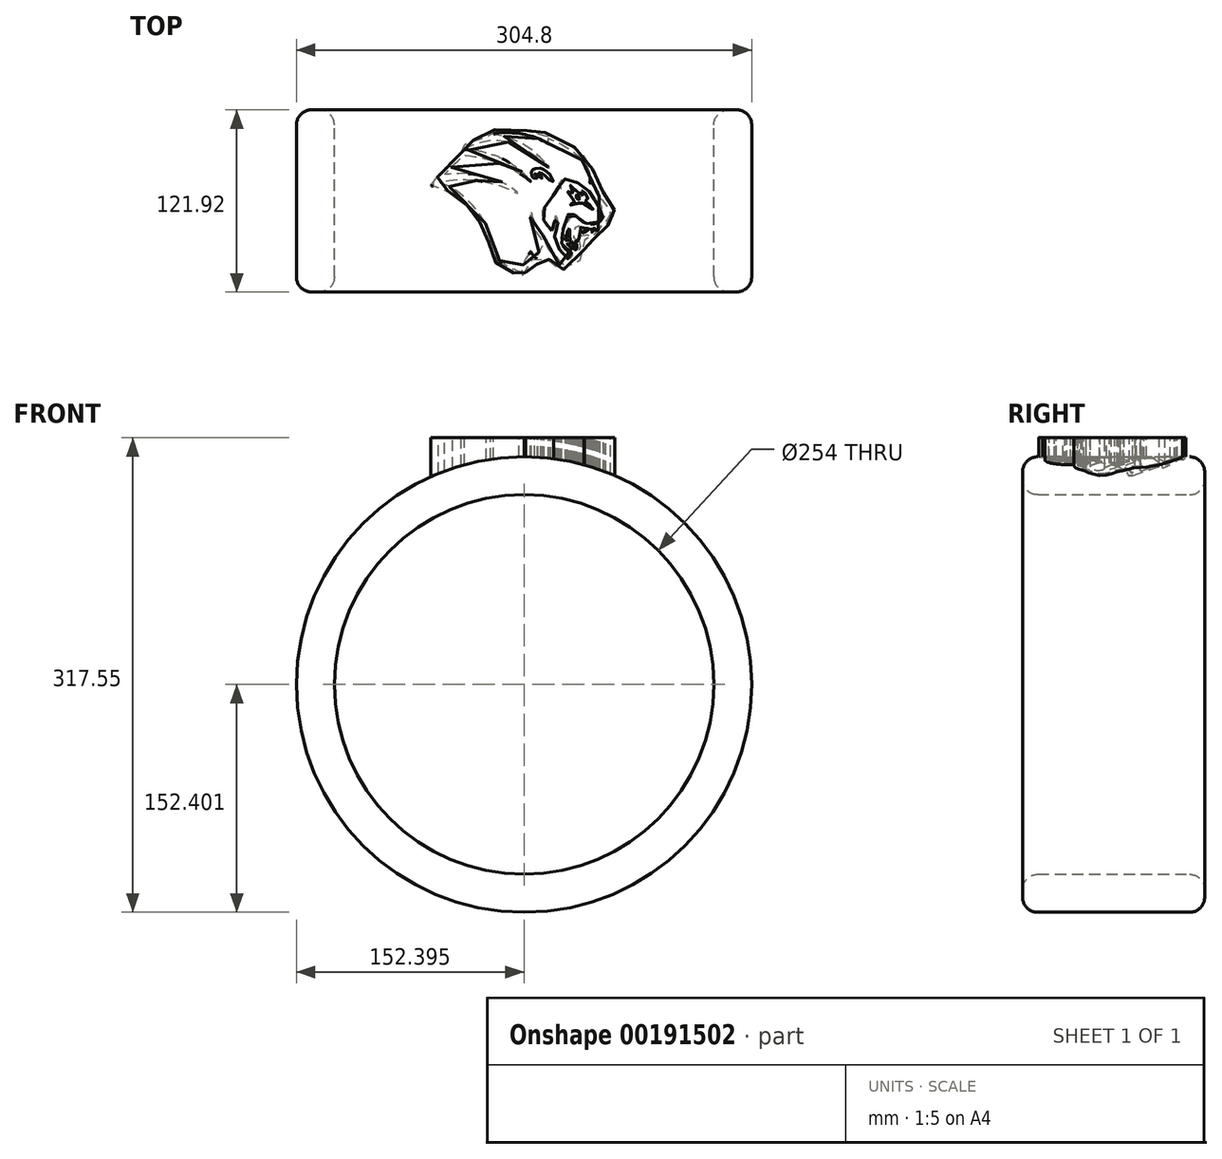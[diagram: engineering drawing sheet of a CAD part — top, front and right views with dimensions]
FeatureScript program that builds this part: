
annotation { "Feature Type Name" : "Feature", "Feature Type Description" : "" }
export const myFeature = defineFeature(function(context is Context, id is Id, definition is map)
    precondition{}
    {
        {
            var Q0;
            Q0=qCreatedBy(makeId("Top.planeOp"),FACE);
            var sketch = newSketch(context, id + "F0", { "sketchPlane" : qUnion([Q0])});
            skFitSpline(sketch, "E0", {"points": [v(-31.09, 27.1) * mm, v(-31.11, 27.15) * mm, v(-36.69, 27.23) * mm, v(-36.69, 27.24) * mm, v(-35.85, 28.2) * mm, v(-34.33, 29.39) * mm, v(-29.23, 32.47) * mm, v(-22.89, 35.49) * mm, v(-13.94, 37.95) * mm, v(-11.34, 38.16) * mm, v(-11.31, 38.2) * mm, v(-14.28, 41.78) * mm, v(-14.26, 41.81) * mm, v(-10.6, 42.33) * mm, v(-7.43, 42.66) * mm, v(-3.17, 42.95) * mm, v(2.4, 43.06) * mm, v(7.16, 42.72) * mm, v(11.67, 42.16) * mm, v(14.33, 41.53) * mm, v(16.85, 40.84) * mm, v(19.9, 39.76) * mm, v(22.88, 38.53) * mm, v(24.4, 37.68) * mm, v(24.45, 37.7) * mm, v(24.02, 40.9) * mm, v(24.02, 40.93) * mm, v(28.38, 39.57) * mm, v(33.53, 37.41) * mm, v(37.52, 35.36) * mm, v(40.75, 33.62) * mm, v(43.89, 31.64) * mm, v(46.7, 29.43) * mm, v(50, 26.6) * mm, v(52.22, 23.95) * mm, v(54.14, 21.65) * mm, v(55.69, 18.98) * mm, v(56.9, 15.92) * mm, v(57.83, 12.7) * mm, v(57.85, 9) * mm, v(57.85, 8.32) * mm, v(57.86, 8.31) * mm, v(60.1, 6.1) * mm, v(61.52, 4.24) * mm, v(63.62, 1.45) * mm, v(65.26, -1.13) * mm, v(65.81, -2.07) * mm, v(65.78, -2.08) * mm, v(65.15, -2.57) * mm, v(65.18, -2.6) * mm, v(66.55, -4.08) * mm, v(68.27, -6.1) * mm, v(69.9, -8.32) * mm, v(71.5, -11.06) * mm, v(71.82, -11.68) * mm, v(71.88, -12.08) * mm, v(71.86, -12.64) * mm, v(71.76, -12.84) * mm, v(71.5, -14.05) * mm, v(71.24, -15.23) * mm, v(70.58, -16.82) * mm, v(69.65, -18.77) * mm, v(68.57, -20.04) * mm, v(67.66, -21.18) * mm, v(66.43, -22.39) * mm, v(65.23, -23.47) * mm, v(63.89, -24.57) * mm, v(63.22, -25.56) * mm, v(62.06, -27.1) * mm, v(60.99, -28.53) * mm, v(59.27, -29.8) * mm, v(57.18, -30.9) * mm, v(54.73, -31.73) * mm, v(52.52, -31.6) * mm, v(50.9, -30.96) * mm, v(50.9, -30.97) * mm, v(50.87, -31.5) * mm, v(51.34, -33.26) * mm, v(51.34, -35.4) * mm, v(51.33, -36.8) * mm, v(50.75, -38.7) * mm, v(49.66, -41.82) * mm, v(48.02, -45.67) * mm, v(44.56, -48.82) * mm, v(40.43, -50.61) * mm, v(37.24, -51.04) * mm, v(34.13, -50.7) * mm, v(30.98, -49.95) * mm, v(30.9, -49.89) * mm, v(32.88, -46.3) * mm, v(32.88, -46.25) * mm, v(28.95, -43.3) * mm, v(28.87, -43.33) * mm, v(28.38, -43.84) * mm, v(27.6, -44.27) * mm, v(26.31, -44.55) * mm, v(24.7, -44.6) * mm, v(22.84, -44.07) * mm, v(21.99, -43.54) * mm, v(21.96, -43.54) * mm, v(21.44, -44.81) * mm, v(20.64, -46.8) * mm, v(20.12, -48.33) * mm, v(20.04, -48.36) * mm, v(18.66, -46.98) * mm, v(17.36, -45.7) * mm, v(16.25, -44.55) * mm, v(15.52, -43.7) * mm, v(15.46, -43.72) * mm, v(14.85, -45.07) * mm, v(13.48, -47.58) * mm, v(12.46, -51.1) * mm, v(12.05, -54.2) * mm, v(12.03, -54.4) * mm, v(11.18, -54.5) * mm, v(11.18, -54.55) * mm, v(11.2, -55.19) * mm, v(11.1, -55.14) * mm, v(10.87, -55.15) * mm, v(8.8, -54.63) * mm, v(7.63, -54.5) * mm, v(6.57, -54.15) * mm, v(5.53, -53.84) * mm, v(4.92, -53.54) * mm, v(3.78, -53.1) * mm, v(2.58, -52.38) * mm, v(2.44, -52.14) * mm, v(0.55, -52.17) * mm, v(-0.92, -51.3) * mm, v(-2.65, -50.3) * mm, v(-4.37, -49.16) * mm, v(-6.14, -47.9) * mm, v(-8.37, -45.72) * mm, v(-8.8, -45.36) * mm, v(-9.07, -44.63) * mm, v(-9.78, -41.7) * mm, v(-10.31, -39.55) * mm, v(-10.83, -37.7) * mm, v(-11.39, -35.7) * mm, v(-12.15, -33.5) * mm, v(-13.05, -31.4) * mm, v(-13.76, -29.67) * mm, v(-14.56, -27.42) * mm, v(-15.32, -25.69) * mm, v(-16.12, -23.85) * mm, v(-16.99, -22.43) * mm, v(-17.61, -20.96) * mm, v(-19.36, -18.15) * mm, v(-20.1, -17.04) * mm, v(-21.13, -15.53) * mm, v(-21.6, -14.82) * mm, v(-23.16, -12.67) * mm, v(-24.28, -11.21) * mm, v(-25.5, -9.91) * mm, v(-26.57, -8.6) * mm, v(-28.06, -7.07) * mm, v(-29.57, -5.48) * mm, v(-31.18, -4.23) * mm, v(-32.48, -3.02) * mm, v(-35.01, -1) * mm, v(-37.93, 0.76) * mm, v(-39.68, 1.63) * mm, v(-43.52, 3.41) * mm, v(-47.16, 4.49) * mm, v(-51.45, 5.15) * mm, v(-51.45, 5.22) * mm, v(-50, 7.18) * mm, v(-47.7, 9.98) * mm, v(-45.1, 13.07) * mm, v(-41.63, 16.66) * mm, v(-37.44, 21.13) * mm, v(-34.27, 24.1) * mm, v(-31.09, 27.1) * mm]});
            skFitSpline(sketch, "E1", {"points": [v(-14.87, -19.96) * mm, v(-16.53, -17.13) * mm, v(-18.86, -13.58) * mm, v(-21.78, -9.61) * mm, v(-24.55, -6.73) * mm, v(-29.24, -2.2) * mm, v(-33.32, 1.06) * mm, v(-37.46, 3.8) * mm, v(-40.9, 5.46) * mm, v(-43.35, 6.3) * mm, v(-45.8, 6.8) * mm, v(-46.1, 7) * mm, v(-45.1, 7.59) * mm, v(-39.68, 8.6) * mm, v(-34.05, 9.1) * mm, v(-26.3, 9.07) * mm, v(-20, 8.52) * mm, v(-11.98, 6.95) * mm, v(-2.95, 4.5) * mm, v(7.46, -0.37) * mm, v(7.58, -0.43) * mm, v(5.39, 1.58) * mm, v(1.22, 4.64) * mm, v(-6.3, 8.72) * mm, v(-13.47, 10.97) * mm, v(-20.35, 12.54) * mm, v(-32.07, 13.18) * mm, v(-42.1, 12.72) * mm, v(-42, 12.83) * mm, v(-37.72, 17.5) * mm, v(-31.7, 23.1) * mm, v(-29.15, 25.2) * mm, v(-24.9, 25.08) * mm, v(-20.47, 24.47) * mm, v(-15.32, 23.36) * mm, v(-11.1, 22.1) * mm, v(-6, 20.24) * mm, v(-1.72, 18.52) * mm, v(2.27, 16.6) * mm, v(8.16, 13.3) * mm, v(13.4, 9.63) * mm, v(15.68, 7.8) * mm, v(15.68, 7.82) * mm, v(14.13, 9.77) * mm, v(12.1, 12.08) * mm, v(8.3, 15.63) * mm, v(5.1, 18.14) * mm, v(0.78, 20.85) * mm, v(-6.8, 24.67) * mm, v(-16.6, 27.67) * mm, v(-19.8, 28.49) * mm, v(-23.88, 28.93) * mm, v(-27.84, 29.13) * mm, v(-28.83, 29.25) * mm, v(-28.25, 30.03) * mm, v(-24.92, 31.85) * mm, v(-18.83, 34.06) * mm, v(-13.56, 35.28) * mm, v(-9.07, 35.69) * mm, v(-3.03, 35.3) * mm, v(3.32, 33.44) * mm, v(8.22, 31.43) * mm, v(14.57, 27.73) * mm, v(19.8, 23.97) * mm, v(25.5, 18.58) * mm, v(29.06, 15.28) * mm, v(29.06, 15.31) * mm, v(27.98, 16.94) * mm, v(25.97, 19.45) * mm, v(22.94, 23.1) * mm, v(19.59, 26.07) * mm, v(16.79, 28.66) * mm, v(12.12, 32.04) * mm, v(7.7, 34.26) * mm, v(0, 37.44) * mm, v(-4.46, 38.57) * mm, v(-9.33, 39.6) * mm, v(-9.3, 39.74) * mm, v(-7.35, 40.32) * mm, v(1.8, 40.56) * mm, v(8.65, 39.94) * mm, v(15.65, 38.31) * mm, v(20.75, 36.65) * mm, v(27.72, 32.86) * mm, v(27.72, 32.89) * mm, v(27.46, 36.7) * mm, v(27.52, 36.77) * mm, v(31.83, 34.93) * mm, v(36.67, 32.57) * mm, v(42.64, 28.75) * mm, v(48.47, 24.06) * mm, v(52.7, 18.98) * mm, v(54.89, 13.8) * mm, v(55.33, 9.69) * mm, v(55.18, 7.18) * mm, v(55.27, 7.1) * mm, v(57.42, 4.85) * mm, v(60.51, 1.35) * mm, v(61.91, -0.72) * mm, v(61.88, -0.8) * mm, v(60.78, -1.71) * mm, v(60.9, -1.8) * mm, v(63.2, -4.3) * mm, v(66.14, -7.78) * mm, v(68.88, -11.92) * mm, v(68.9, -13.05) * mm, v(68.27, -15.24) * mm, v(66.37, -18.42) * mm, v(63.66, -21.24) * mm, v(62.06, -22.18) * mm, v(62.03, -22.43) * mm, v(60.9, -24.65) * mm, v(58.62, -26.9) * mm, v(55.24, -28.88) * mm, v(52.93, -29.11) * mm, v(52.9, -28.97) * mm, v(54.07, -26.96) * mm, v(53.95, -27.07) * mm, v(52.2, -28.1) * mm, v(50.31, -28.74) * mm, v(46.46, -28.82) * mm, v(46.5, -28.65) * mm, v(49.67, -22.96) * mm, v(49.32, -22.67) * mm, v(48.18, -21.97) * mm, v(47.13, -20.96) * mm, v(47.05, -20.96) * mm, v(46.7, -21.42) * mm, v(45.15, -23.14) * mm, v(44.22, -23.85) * mm, v(44.1, -24.19) * mm, v(44.19, -29.7) * mm, v(44.22, -29.7) * mm, v(44.92, -28.76) * mm, v(44.95, -28.8) * mm, v(45.44, -29.35) * mm, v(45.8, -30.37) * mm, v(45.9, -32.23) * mm, v(46, -32.23) * mm, v(47.48, -30.69) * mm, v(47.54, -30.69) * mm, v(47.98, -31.21) * mm, v(48.42, -32.87) * mm, v(48.68, -36.43) * mm, v(47.54, -38.62) * mm, v(47.37, -39.43) * mm, v(46.46, -42.26) * mm, v(44.66, -45.2) * mm, v(41.97, -47.1) * mm, v(38.65, -48.03) * mm, v(34.77, -47.92) * mm, v(34.74, -47.86) * mm, v(36.17, -45.32) * mm, v(36.17, -45.26) * mm, v(34.07, -43.66) * mm, v(30.98, -41.07) * mm, v(29.12, -39.32) * mm, v(27.14, -36.66) * mm, v(26.2, -34.83) * mm, v(25.45, -32.87) * mm, v(24.9, -30.05) * mm, v(24.75, -28.85) * mm, v(24.66, -28.8) * mm, v(23.29, -27.54) * mm, v(21.74, -25.69) * mm, v(20.52, -23.85) * mm, v(18.68, -20.22) * mm, v(17.37, -17.45) * mm, v(16.55, -14.63) * mm, v(15.91, -12.2) * mm, v(15.77, -9.76) * mm, v(15.68, -9.76) * mm, v(15.36, -12.64) * mm, v(15.27, -16.23) * mm, v(16.12, -20.1) * mm, v(17.46, -23.43) * mm, v(19.24, -26.14) * mm, v(22.06, -29.32) * mm, v(22.27, -29.52) * mm, v(22.3, -30.95) * mm, v(22.73, -33.22) * mm, v(23.96, -35.85) * mm, v(23.93, -36) * mm, v(22.82, -36.98) * mm, v(20.93, -39.55) * mm, v(19.88, -41.24) * mm, v(19.24, -43.28) * mm, v(19.1, -43.4) * mm, v(18.57, -43.08) * mm, v(17.87, -42.17) * mm, v(17.08, -41.15) * mm, v(16.06, -39.6) * mm, v(15.65, -38.9) * mm, v(15.62, -38.94) * mm, v(14.51, -40.3) * mm, v(13.32, -42.03) * mm, v(11.95, -44.27) * mm, v(11.07, -46.34) * mm, v(10.35, -48.41) * mm, v(9.62, -50.86) * mm, v(9.35, -52.58) * mm, v(9.3, -52.58) * mm, v(7.52, -52.23) * mm, v(6.06, -51.74) * mm, v(4.14, -50.95) * mm, v(2.62, -50.28) * mm, v(0.46, -49.2) * mm, v(-0.88, -48.32) * mm, v(-2.69, -47.13) * mm, v(-4.06, -46.14) * mm, v(-5.37, -45) * mm, v(-6.5, -43.86) * mm, v(-7.09, -43.08) * mm, v(-7.35, -41.82) * mm, v(-7.58, -39.96) * mm, v(-8.43, -37.07) * mm, v(-9.27, -34.13) * mm, v(-10.79, -29.55) * mm, v(-12.22, -25.9) * mm, v(-14.26, -21.53) * mm, v(-14.87, -19.96) * mm]});
            skFitSpline(sketch, "E2", {"points": [v(20.64, 14.12) * mm, v(21.76, 13.88) * mm, v(23.17, 13.2) * mm, v(24.26, 12.5) * mm, v(25.27, 11.74) * mm, v(26.44, 10.52) * mm, v(27.07, 9.84) * mm, v(27.64, 9.1) * mm, v(27.7, 9.06) * mm, v(30.4, 7.75) * mm, v(30.5, 7.73) * mm, v(30.46, 7.97) * mm, v(30.13, 9) * mm, v(29.51, 10.69) * mm, v(28.86, 12.03) * mm, v(27.76, 13.35) * mm, v(26.8, 14.2) * mm, v(25.54, 15.12) * mm, v(24.24, 15.9) * mm, v(23, 16.5) * mm, v(21.47, 16.84) * mm, v(19.08, 16.75) * mm, v(17.8, 16.44) * mm, v(16.92, 15.9) * mm, v(16.42, 15.22) * mm, v(16.11, 14.43) * mm, v(15.98, 12.98) * mm, v(16.3, 11.89) * mm, v(16.76, 11.13) * mm, v(17.4, 10.34) * mm, v(17.5, 10.21) * mm, v(20.2, 10.12) * mm, v(20.2, 10.16) * mm, v(20, 10.47) * mm, v(19.46, 11.3) * mm, v(18.95, 11.9) * mm, v(18.42, 12.67) * mm, v(18.18, 13.08) * mm, v(18.18, 13.1) * mm, v(18.77, 12.97) * mm, v(20.42, 12.07) * mm, v(21.6, 11.22) * mm, v(23.34, 10) * mm, v(23.4, 10.01) * mm, v(23.45, 10.34) * mm, v(22.77, 11.31) * mm, v(21.82, 12.43) * mm, v(21.06, 13.19) * mm, v(20.47, 13.8) * mm, v(20.36, 14.07) * mm, v(20.64, 14.12) * mm]});
            skFitSpline(sketch, "E3", {"points": [v(29.5, -24.96) * mm, v(28.58, -24.35) * mm, v(27.6, -23.28) * mm, v(26.55, -21.99) * mm, v(25.54, -20.52) * mm, v(24.7, -18.86) * mm, v(23.88, -16.81) * mm, v(23.47, -15.09) * mm, v(22.99, -12.75) * mm, v(23.1, -12.53) * mm, v(23.95, -10.91) * mm, v(24.86, -9.04) * mm, v(25.75, -7.35) * mm, v(26.7, -5.8) * mm, v(27.88, -4.41) * mm, v(29.43, -2.66) * mm, v(31.27, -0.9) * mm, v(33.27, 0.81) * mm, v(35.98, 3.21) * mm, v(35.98, 3.28) * mm, v(35.63, 3.76) * mm, v(35.07, 4.35) * mm, v(34.8, 4.96) * mm, v(34.63, 5.81) * mm, v(34.7, 7.06) * mm, v(34.93, 7.73) * mm, v(35.94, 8.78) * mm, v(36.81, 9.33) * mm, v(38.01, 9.61) * mm, v(39.35, 9.66) * mm, v(40.85, 9.42) * mm, v(42.3, 9.1) * mm, v(43.98, 8.55) * mm, v(45.84, 7.68) * mm, v(47.83, 6.54) * mm, v(49.9, 5.2) * mm, v(51.6, 3.98) * mm, v(52.98, 2.8) * mm, v(53.93, 1.93) * mm, v(55, 0.77) * mm, v(56.05, -0.54) * mm, v(56.03, -0.56) * mm, v(54.65, -1.24) * mm, v(54.76, -1.3) * mm, v(56.03, -2.2) * mm, v(57.65, -3.42) * mm, v(59.34, -4.88) * mm, v(61.47, -7.1) * mm, v(63.04, -8.9) * mm, v(64.22, -10.48) * mm, v(64.2, -10.5) * mm, v(59.74, -11.02) * mm, v(59.72, -11.02) * mm, v(59.74, -11.42) * mm, v(59.9, -11.48) * mm, v(60.57, -11.75) * mm, v(62.04, -12.36) * mm, v(62.65, -12.6) * mm, v(62.67, -12.62) * mm, v(62.71, -13.34) * mm, v(62.89, -13.71) * mm, v(63.48, -14.6) * mm, v(64.22, -15.52) * mm, v(64.24, -15.74) * mm, v(63.94, -16.3) * mm, v(63.43, -17) * mm, v(62.73, -17.9) * mm, v(61.93, -18.67) * mm, v(60.8, -19.43) * mm, v(59.6, -19.98) * mm, v(58.43, -20.37) * mm, v(57.17, -20.61) * mm, v(54.26, -20.46) * mm, v(52.54, -20.04) * mm, v(51.49, -19.56) * mm, v(49.87, -18.62) * mm, v(48.5, -17.51) * mm, v(47.3, -16.44) * mm, v(45.88, -15.17) * mm, v(44.76, -14.52) * mm, v(44.04, -14.3) * mm, v(41.64, -14.17) * mm, v(40.04, -14.54) * mm, v(39.04, -15.41) * mm, v(39.08, -15.44) * mm, v(41.8, -16.57) * mm, v(41.82, -16.65) * mm, v(40.93, -18) * mm, v(39.82, -19.8) * mm, v(38.1, -22.76) * mm, v(36.88, -24.94) * mm, v(36.12, -27.16) * mm, v(35.87, -29.14) * mm, v(35.87, -32.06) * mm, v(36.24, -33.32) * mm, v(37, -35.08) * mm, v(38.26, -36.67) * mm, v(39.49, -37.84) * mm, v(41.2, -39.1) * mm, v(42.76, -39.92) * mm, v(43.55, -40.27) * mm, v(43.61, -40.33) * mm, v(43.34, -41.19) * mm, v(42.78, -42.37) * mm, v(41.7, -43.5) * mm, v(39.96, -44.59) * mm, v(39.96, -44.57) * mm, v(40.25, -43.87) * mm, v(40.3, -43.77) * mm, v(39.86, -43.27) * mm, v(38.83, -42.37) * mm, v(37.58, -41.13) * mm, v(36.04, -39.4) * mm, v(34.86, -37.76) * mm, v(33.78, -36.12) * mm, v(32.58, -33.71) * mm, v(31.7, -31.43) * mm, v(31.06, -29.18) * mm, v(31.06, -29.1) * mm, v(31.73, -28.48) * mm, v(32.62, -26.8) * mm, v(33.3, -25.15) * mm, v(33.67, -23.64) * mm, v(33.9, -21.67) * mm, v(33.87, -19.43) * mm, v(33.67, -17.84) * mm, v(33.1, -16.36) * mm, v(31.92, -14.6) * mm, v(31.92, -14.67) * mm, v(31.88, -16.13) * mm, v(31.92, -18.77) * mm, v(31.78, -19.78) * mm, v(31.5, -21.26) * mm, v(31.1, -22.48) * mm, v(30.62, -23.69) * mm, v(29.88, -24.82) * mm, v(29.5, -24.96) * mm]});
            skFitSpline(sketch, "E4", {"points": [v(40.24, 1.17) * mm, v(41.09, 1.11) * mm, v(42.05, 0.77) * mm, v(43.01, 0.27) * mm, v(43.68, -0.31) * mm, v(43.77, -0.37) * mm, v(43.8, 1) * mm, v(43.65, 1.35) * mm, v(43.27, 2.1) * mm, v(42.6, 3.4) * mm, v(41.96, 5.37) * mm, v(42.05, 5.43) * mm, v(42.72, 4.67) * mm, v(43.89, 3.5) * mm, v(45.58, 2.16) * mm, v(47.44, 0.68) * mm, v(50.56, -1.77) * mm, v(50.56, -1.74) * mm, v(50.45, -0.63) * mm, v(50.15, 0.77) * mm, v(49.98, 1.84) * mm, v(50.04, 1.9) * mm, v(50.82, 1.2) * mm, v(51.79, 0.27) * mm, v(52.9, -1.04) * mm, v(54.06, -3.64) * mm, v(54.03, -3.78) * mm, v(52.34, -5.3) * mm, v(52.34, -5.56) * mm, v(53.83, -6.4) * mm, v(55.81, -8.48) * mm, v(57.2, -10.46) * mm, v(57.3, -10.9) * mm, v(57.15, -10.95) * mm, v(56.5, -10.6) * mm, v(55.46, -9.76) * mm, v(54.32, -8.94) * mm, v(53.22, -8.24) * mm, v(51.82, -7.43) * mm, v(50.53, -6.81) * mm, v(50.07, -6.7) * mm, v(49.2, -6.64) * mm, v(47.82, -6.7) * mm, v(46.04, -6.93) * mm, v(44.1, -7.43) * mm, v(42.23, -7.8) * mm, v(42.14, -7.63) * mm, v(42.63, -6.81) * mm, v(44.1, -6.17) * mm, v(45, -5.76) * mm, v(44.47, -4.51) * mm, v(43.71, -3.37) * mm, v(42.34, -1.65) * mm, v(41.18, -0.43) * mm, v(40.45, 0.39) * mm, v(40.13, 0.85) * mm, v(40.24, 1.17) * mm]});
            skFitSpline(sketch, "E5", {"points": [v(48.03, -4.49) * mm, v(47.18, -3.97) * mm, v(46.38, -3.42) * mm, v(46.08, -2.9) * mm, v(46.05, -0.97) * mm, v(46.13, -0.94) * mm, v(46.66, -1.3) * mm, v(47.37, -1.8) * mm, v(48.06, -2.23) * mm, v(48.39, -2.43) * mm, v(48.06, -2.67) * mm, v(47.54, -2.65) * mm, v(47.43, -2.67) * mm, v(47.43, -2.76) * mm, v(47.4, -3.25) * mm, v(47.43, -3.55) * mm, v(47.7, -3.83) * mm, v(48.14, -4.02) * mm, v(48.03, -4.49) * mm]});
            skFitSpline(sketch, "E6", {"points": [v(41.23, -23.47) * mm, v(41.46, -24.03) * mm, v(41.64, -25.4) * mm, v(41.84, -27.4) * mm, v(41.93, -30.8) * mm, v(41.87, -31.43) * mm, v(38.93, -31.37) * mm, v(38.93, -31.29) * mm, v(39.07, -27.96) * mm, v(39.25, -28.05) * mm, v(40.36, -29.48) * mm, v(40.39, -29.42) * mm, v(40.36, -28.28) * mm, v(39.89, -26.5) * mm, v(39.86, -26.36) * mm, v(41.23, -23.47) * mm]});
            skFitSpline(sketch, "E7", {"points": [v(43.9, -32.26) * mm, v(44, -32.68) * mm, v(44.06, -33.62) * mm, v(43.9, -34.76) * mm, v(43.35, -35.63) * mm, v(42.63, -36.29) * mm, v(42.63, -36.3) * mm, v(42.32, -36.03) * mm, v(41.2, -35.1) * mm, v(39.9, -33.9) * mm, v(39.92, -33.86) * mm, v(40.22, -33.86) * mm, v(40.8, -33.82) * mm, v(41.58, -33.76) * mm, v(42.32, -33.48) * mm, v(42.75, -33.17) * mm, v(43.15, -32.85) * mm, v(43.58, -32.5) * mm, v(43.9, -32.26) * mm]});
            skFitSpline(sketch, "E8", {"points": [v(46.23, -34.05) * mm, v(46.4, -34.33) * mm, v(46.52, -35.02) * mm, v(46.56, -35.81) * mm, v(46.49, -36.61) * mm, v(46.13, -37.18) * mm, v(45.84, -37.73) * mm, v(45.76, -37.78) * mm, v(44.6, -37.15) * mm, v(44.66, -37.12) * mm, v(44.97, -36.67) * mm, v(45.26, -36.12) * mm, v(45.58, -35.55) * mm, v(45.77, -35) * mm, v(46.02, -34.42) * mm, v(46.23, -34.05) * mm]});
            skFitSpline(sketch, "E9", {"points": [v(51.94, -23.4) * mm, v(51.97, -23.4) * mm, v(54.59, -23.63) * mm, v(54.6, -23.67) * mm, v(54.33, -24.06) * mm, v(54.08, -24.42) * mm, v(53.72, -24.74) * mm, v(53.35, -25.08) * mm, v(52.74, -25.44) * mm, v(52.09, -25.8) * mm, v(51.43, -26.09) * mm, v(50.34, -26.57) * mm, v(50.32, -26.56) * mm, v(50.68, -25.97) * mm, v(51.02, -25.37) * mm, v(51.35, -24.76) * mm, v(51.65, -24.1) * mm, v(51.94, -23.4) * mm]});
            skFitSpline(sketch, "E10", {"points": [v(57.17, -23.8) * mm, v(57.17, -23.53) * mm, v(57.52, -23.47) * mm, v(58.72, -23.46) * mm, v(58.73, -23.5) * mm, v(58.65, -23.82) * mm, v(58.34, -24.36) * mm, v(57.93, -24.82) * mm, v(57.38, -25.38) * mm, v(56.9, -25.72) * mm, v(56.31, -26.04) * mm, v(56.31, -26.03) * mm, v(56.48, -25.58) * mm, v(56.7, -25.08) * mm, v(56.93, -24.65) * mm, v(57.07, -24.23) * mm, v(57.17, -23.8) * mm]});
            skSolve(sketch);
        }
        {
            var Q0;
            Q0=makeQuery(id+"F0.imprint","IMPRINT",FACE,{"disambiguationData":[TD([[makeQuery(id+"F0.imprint","IMPRINT",EDGE,{"derivedFrom":sQuery(id+"F0.wireOp",EDGE,"E3")}),-1.0]])]});
            var Q1;
            Q1=makeQuery(id+"F0.imprint","IMPRINT",FACE,{"disambiguationData":[TD([[makeQuery(id+"F0.imprint","IMPRINT",EDGE,{"derivedFrom":sQuery(id+"F0.wireOp",EDGE,"E0")}),-1.0]])]});
            var Q2;
            Q2=makeQuery(id+"F0.imprint","IMPRINT",FACE,{"disambiguationData":[TD([[makeQuery(id+"F0.imprint","IMPRINT",EDGE,{"derivedFrom":sQuery(id+"F0.wireOp",EDGE,"E6")}),-1.0]])]});
            var Q3;
            Q3=makeQuery(id+"F0.imprint","IMPRINT",FACE,{"disambiguationData":[TD([[makeQuery(id+"F0.imprint","IMPRINT",EDGE,{"derivedFrom":sQuery(id+"F0.wireOp",EDGE,"E2")}),1.0]])]});
            var Q4;
            Q4=makeQuery(id+"F0.imprint","IMPRINT",FACE,{"disambiguationData":[TD([[makeQuery(id+"F0.imprint","IMPRINT",EDGE,{"derivedFrom":sQuery(id+"F0.wireOp",EDGE,"E9")}),-1.0]])]});
            var Q5;
            Q5=makeQuery(id+"F0.imprint","IMPRINT",FACE,{"disambiguationData":[TD([[makeQuery(id+"F0.imprint","IMPRINT",EDGE,{"derivedFrom":sQuery(id+"F0.wireOp",EDGE,"E7")}),-1.0]])]});
            var Q6;
            Q6=makeQuery(id+"F0.imprint","IMPRINT",FACE,{"disambiguationData":[TD([[makeQuery(id+"F0.imprint","IMPRINT",EDGE,{"derivedFrom":sQuery(id+"F0.wireOp",EDGE,"E5")}),-1.0]])]});
            var Q7;
            Q7=makeQuery(id+"F0.imprint","IMPRINT",FACE,{"disambiguationData":[TD([[makeQuery(id+"F0.imprint","IMPRINT",EDGE,{"derivedFrom":sQuery(id+"F0.wireOp",EDGE,"E10")}),-1.0]])]});
            var Q8;
            Q8=makeQuery(id+"F0.imprint","IMPRINT",FACE,{"disambiguationData":[TD([[makeQuery(id+"F0.imprint","IMPRINT",EDGE,{"derivedFrom":sQuery(id+"F0.wireOp",EDGE,"E8")}),-1.0]])]});
            extrude(context, id + "F1", {"entities" : qUnion([Q0, Q1, Q2, Q3, Q4, Q5, Q6, Q7, Q8]), "depth" : 25.4 * mm});
        }
        {
            var Q0;
            Q0=qCreatedBy(makeId("Front.planeOp"),FACE);
            var sketch = newSketch(context, id + "F2", { "sketchPlane" : qUnion([Q0])});
            skLineSegment(sketch, "E11", {"start": v(11.15, 12.65) * mm, "end": v(-46, 12.65) * mm});
            skPoint(sketch, "E12", {"position": v(11.15, 12.65) * mm});
            skSolve(sketch);
        }
        {
            var Q0;
            Q0=qCreatedBy(makeId("Front.planeOp"),FACE);
            cPlane(context, id + "F3", {"entities" : qUnion([Q0]), "cplaneType" : CPlaneType.OFFSET, "offset" : 76.2 * mm, "width" : 152.4 * mm, "height" : 152.4 * mm});
        }
        {
            var Q0;
            Q0=qCreatedBy(id+"F3.planeOp",FACE);
            var sketch = newSketch(context, id + "F4", { "sketchPlane" : qUnion([Q0])});
            skCircle(sketch, "E13", {"center": v(11.15, -139.75) * mm, "radius": 152.4 * mm});
            skSolve(sketch);
        }
        {
            var Q0;
            Q0=makeQuery(id+"F4.imprint","IMPRINT",FACE,{"disambiguationData":[TD([[makeQuery(id+"F4.imprint","IMPRINT",EDGE,{"derivedFrom":sQuery(id+"F4.wireOp",EDGE,"E13")}),1.0]])]});
            extrude(context, id + "F5", {"entities" : qUnion([Q0]), "operationType" : NewBodyOperationType.REMOVE, "oppositeDirection" : true, "depth" : 254 * mm});
        }
        {
            var Q0;
            Q0=qCreatedBy(makeId("Front.planeOp"),FACE);
            cPlane(context, id + "F6", {"entities" : qUnion([Q0]), "cplaneType" : CPlaneType.OFFSET, "offset" : 55.88 * mm, "oppositeDirection" : true, "width" : 152.4 * mm, "height" : 152.4 * mm});
        }
        {
            var Q0;
            Q0=qCreatedBy(id+"F6.planeOp",FACE);
            var sketch = newSketch(context, id + "F7", { "sketchPlane" : qUnion([Q0])});
            skCircle(sketch, "E14", {"center": v(11.15, -139.75) * mm, "radius": 152.4 * mm});
            skCircle(sketch, "E15", {"center": v(11.15, -139.75) * mm, "radius": 127 * mm});
            skSolve(sketch);
        }
        {
            var Q0;
            Q0=makeQuery(id+"F7.imprint","IMPRINT",FACE,{"disambiguationData":[TD([[makeQuery(id+"F7.imprint","IMPRINT",EDGE,{"derivedFrom":sQuery(id+"F7.wireOp",EDGE,"E14")}),1.0]])]});
            extrude(context, id + "F8", {"entities" : qUnion([Q0]), "depth" : 121.92 * mm});
        }
        {
            var Q0;
            Q0=makeQuery(id+"F8.opExtrude","CAP_EDGE",EDGE,{"disambiguationData":[OSD([sQuery(id+"F7.wireOp",EDGE,"E14")])],"isStart":true});
            var Q1;
            Q1=makeQuery(id+"F8.opExtrude","CAP_EDGE",EDGE,{"disambiguationData":[OSD([sQuery(id+"F7.wireOp",EDGE,"E15")])],"isStart":true});
            var Q2;
            Q2=makeQuery(id+"F8.opExtrude","CAP_EDGE",EDGE,{"disambiguationData":[OSD([sQuery(id+"F7.wireOp",EDGE,"E14")])],"isStart":false});
            var Q3;
            Q3=makeQuery(id+"F8.opExtrude","CAP_EDGE",EDGE,{"disambiguationData":[OSD([sQuery(id+"F7.wireOp",EDGE,"E15")])],"isStart":false});
            fillet(context, id + "F9", {"entities" : qUnion([Q0, Q1, Q2, Q3]), "radius" : 10.16 * mm, "tangentPropagation" : true, "allowEdgeOverflow" : false});
        }
    });
